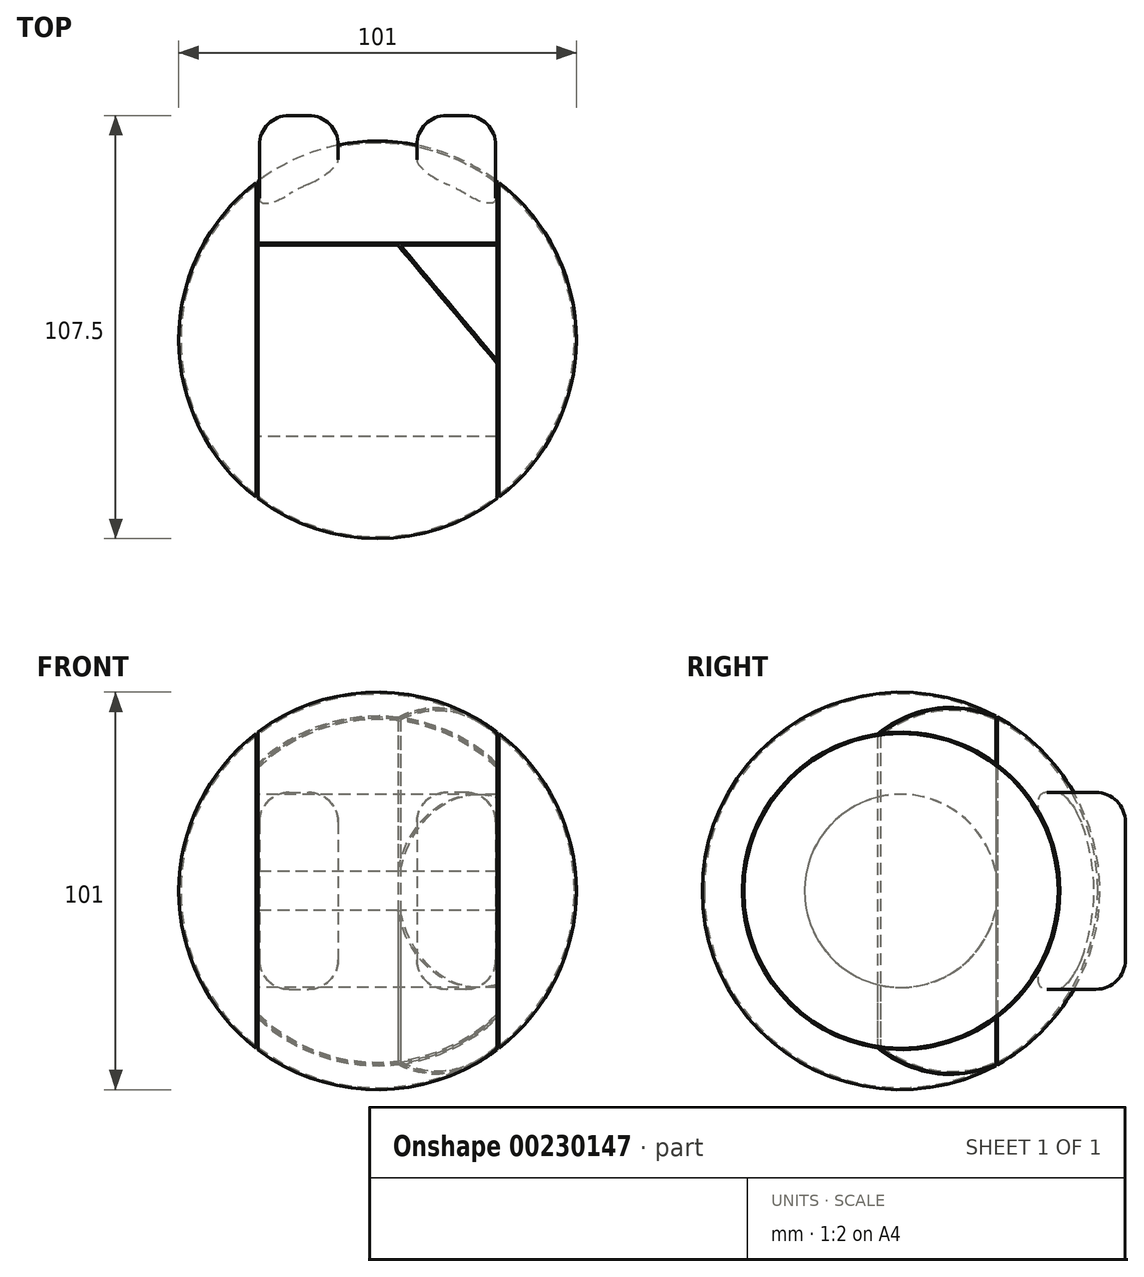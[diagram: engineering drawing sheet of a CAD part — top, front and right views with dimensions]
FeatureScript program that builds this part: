
annotation { "Feature Type Name" : "Feature", "Feature Type Description" : "" }
export const myFeature = defineFeature(function(context is Context, id is Id, definition is map)
    precondition{}
    {
        {
            var Q0;
            Q0=qCreatedBy(makeId("Top.planeOp"),FACE);
            var sketch = newSketch(context, id + "F0", { "sketchPlane" : qUnion([Q0])});
            skCircle(sketch, "E0", {"center": v(0, 0) * mm, "radius": 50 * mm});
            skLineSegment(sketch, "E1", {"start": v(0, 50) * mm, "end": v(0, -50) * mm});
            skSolve(sketch);
        }
        {
            var Q0;
            {var subQ0=sQuery(id+"F0.wireOp",EDGE,"E1");Q0=makeQuery(id+"F0.imprint","IMPRINT",FACE,{"disambiguationData":[TD([[makeQuery(id+"F0.imprint","IMPRINT",EDGE,{"derivedFrom":subQ0}),-1.0]])]});}
            var Q1;
            Q1=sQuery(id+"F0.wireOp",EDGE,"E1");
            revolve(context, id + "F1", {"entities" : qUnion([Q0]), "axis" : qUnion([Q1]), "revolveType" : RevolveType.FULL});
        }
        {
            var Q0;
            Q0=qCreatedBy(makeId("Front.planeOp"),FACE);
            var sketch = newSketch(context, id + "F2", { "sketchPlane" : qUnion([Q0])});
            skCircle(sketch, "E2", {"center": v(0, 0) * mm, "radius": 50 * mm});
            skLineSegment(sketch, "E3", {"start": v(22.5, 25) * mm, "end": v(-43.3, 25) * mm, "construction": true});
            skLineSegment(sketch, "E4", {"start": v(0, 50) * mm, "end": v(0, -50) * mm, "construction": true});
            skLineSegment(sketch, "E5", {"start": v(50, 0) * mm, "end": v(-50, 0) * mm, "construction": true});
            skLineSegment(sketch, "E6.bottom", {"start": v(30, 25) * mm, "end": v(17.5, 25) * mm});
            skLineSegment(sketch, "E6.top", {"start": v(22.5, -25) * mm, "end": v(17.5, -25) * mm});
            skLineSegment(sketch, "E6.left", {"start": v(30, 17.5) * mm, "end": v(30, -17.5) * mm});
            skLineSegment(sketch, "E6.right", {"start": v(10, 17.5) * mm, "end": v(10, -17.5) * mm});
            skPoint(sketch, "E7.newPointA", {"position": v(30, 25) * mm});
            skArc(sketch, "E7.filletArc", {"start": v(30, 17.5) * mm, "mid": v(27.8, 22.8) * mm, "end": v(22.5, 25) * mm});
            skPoint(sketch, "E8.visualSharp", {"position": v(10, 25) * mm});
            skArc(sketch, "E8.filletArc", {"start": v(17.5, 25) * mm, "mid": v(12.2, 22.8) * mm, "end": v(10, 17.5) * mm});
            skPoint(sketch, "E9.visualSharp", {"position": v(30, -25) * mm});
            skArc(sketch, "E9.filletArc", {"start": v(22.5, -25) * mm, "mid": v(27.8, -22.8) * mm, "end": v(30, -17.5) * mm});
            skPoint(sketch, "E10.visualSharp", {"position": v(10, -25) * mm});
            skArc(sketch, "E10.filletArc", {"start": v(10, -17.5) * mm, "mid": v(12.2, -22.8) * mm, "end": v(17.5, -25) * mm});
            skLineSegment(sketch, "E11.MirrorCS", {"start": v(-10, 17.5) * mm, "end": v(-10, -17.5) * mm});
            skLineSegment(sketch, "E12.MirrorCS", {"start": v(-30, 17.5) * mm, "end": v(-30, -17.5) * mm});
            skArc(sketch, "E13.MirrorCS", {"start": v(-30, 17.5) * mm, "mid": v(-27.8, 22.8) * mm, "end": v(-22.5, 25) * mm});
            skArc(sketch, "E14.MirrorCS", {"start": v(-17.5, 25) * mm, "mid": v(-12.2, 22.8) * mm, "end": v(-10, 17.5) * mm});
            skArc(sketch, "E15.MirrorCS", {"start": v(-22.5, -25) * mm, "mid": v(-27.8, -22.8) * mm, "end": v(-30, -17.5) * mm});
            skArc(sketch, "E16.MirrorCS", {"start": v(-10, -17.5) * mm, "mid": v(-12.2, -22.8) * mm, "end": v(-17.5, -25) * mm});
            skLineSegment(sketch, "E17.MirrorCS", {"start": v(-22.5, -25) * mm, "end": v(-17.5, -25) * mm});
            skLineSegment(sketch, "E18.MirrorCS", {"start": v(-30, 25) * mm, "end": v(-17.5, 25) * mm});
            skSolve(sketch);
        }
        {
            var Q0;
            Q0=makeQuery(id+"F2.imprint","IMPRINT",FACE,{"disambiguationData":[TD([[makeQuery(id+"F2.imprint","IMPRINT",EDGE,{"derivedFrom":sQuery(id+"F2.wireOp",EDGE,"E6.left")}),-1.0]])]});
            var Q1;
            Q1=makeQuery(id+"F2.imprint","IMPRINT",FACE,{"disambiguationData":[TD([[makeQuery(id+"F2.imprint","IMPRINT",EDGE,{"derivedFrom":sQuery(id+"F2.wireOp",EDGE,"E11.MirrorCS")}),-1.0]])]});
            extrude(context, id + "F3", {"entities" : qUnion([Q0, Q1]), "operationType" : NewBodyOperationType.ADD, "oppositeDirection" : true, "depth" : 57 * mm});
        }
        {
            var Q0;
            Q0=makeQuery(id+"F3.opExtrude","CAP_EDGE",EDGE,{"disambiguationData":[OSD([sQuery(id+"F2.wireOp",EDGE,"E6.right")])],"isStart":false});
            var Q1;
            Q1=makeQuery(id+"F3.opExtrude","CAP_EDGE",EDGE,{"disambiguationData":[OSD([sQuery(id+"F2.wireOp",EDGE,"E12.MirrorCS")])],"isStart":false});
            fillet(context, id + "F4", {"entities" : qUnion([Q0, Q1]), "radius" : 7.5 * mm, "tangentPropagation" : true, "allowEdgeOverflow" : false});
        }
        {
            var Q0;
            Q0=qCreatedBy(makeId("Top.planeOp"),FACE);
            var sketch = newSketch(context, id + "F5", { "sketchPlane" : qUnion([Q0])});
            skCircle(sketch, "E19", {"center": v(0, 0) * mm, "radius": 50.5 * mm});
            skLineSegment(sketch, "E20", {"start": v(0, 50.5) * mm, "end": v(0, -50.5) * mm, "construction": true});
            skLineSegment(sketch, "E21", {"start": v(-30.89, 39.95) * mm, "end": v(-30.89, -39.95) * mm});
            skLineSegment(sketch, "E22", {"start": v(-30.39, 40.33) * mm, "end": v(-30.39, -40.33) * mm});
            skLineSegment(sketch, "E23", {"start": v(-50.5, 0) * mm, "end": v(50.5, 0) * mm, "construction": true});
            skPoint(sketch, "E23.startSnap0", {"position": v(-30.39, 0) * mm});
            skLineSegment(sketch, "E24", {"start": v(-50.5, 0) * mm, "end": v(50.5, 0) * mm});
            skLineSegment(sketch, "E25.MirrorCS", {"start": v(30.39, 40.33) * mm, "end": v(30.39, -40.33) * mm});
            skLineSegment(sketch, "E26.MirrorCS", {"start": v(30.89, 39.95) * mm, "end": v(30.89, -39.95) * mm});
            skLineSegment(sketch, "E27", {"start": v(-30.39, 24.54) * mm, "end": v(30.39, 24.54) * mm});
            skLineSegment(sketch, "E28", {"start": v(-30.39, 24.04) * mm, "end": v(30.39, 24.04) * mm});
            skLineSegment(sketch, "E29", {"start": v(5.85, 24.04) * mm, "end": v(30.39, -5.24) * mm});
            skLineSegment(sketch, "E30", {"start": v(5.2, 24.04) * mm, "end": v(30.39, -6.02) * mm});
            skSolve(sketch);
        }
        {
            var Q0;
            {var subQ0=sQuery(id+"F5.wireOp",EDGE,"E21");var subQ1=sQuery(id+"F5.wireOp",EDGE,"E19");var subQ2=makeQuery(id+"F5.imprint","INTERSECT",VERTEX,{"disambiguationData":[OD(0.0)],"derivedFrom":[subQ1,subQ0]});Q0=makeQuery(id+"F5.imprint","IMPRINT",FACE,{"disambiguationData":[TD([[makeQuery(id+"F5.imprint","IMPRINT",EDGE,{"disambiguationData":[TD([[subQ2,-1.0]])],"derivedFrom":subQ1}),1.0]])]});}
            var Q1;
            {var subQ0=sQuery(id+"F5.wireOp",EDGE,"E24");var subQ1=sQuery(id+"F5.wireOp",EDGE,"E19");var subQ2=makeQuery(id+"F5.imprint","INTERSECT",VERTEX,{"disambiguationData":[OD(1.0)],"derivedFrom":[subQ1,subQ0]});Q1=makeQuery(id+"F5.imprint","IMPRINT",FACE,{"disambiguationData":[TD([[makeQuery(id+"F5.imprint","IMPRINT",EDGE,{"disambiguationData":[TD([[subQ2,-1.0]])],"derivedFrom":subQ1}),1.0]])]});}
            var Q2;
            {var subQ5=sQuery(id+"F5.wireOp",EDGE,"E27");Q2=makeQuery(id+"F5.imprint","IMPRINT",FACE,{"disambiguationData":[TD([[makeQuery(id+"F5.imprint","IMPRINT",EDGE,{"derivedFrom":subQ5}),1.0]])]});}
            var Q3;
            Q3=sQuery(id+"F5.wireOp",EDGE,"E24");
            revolve(context, id + "F6", {"entities" : qUnion([Q0, Q1, Q2]), "axis" : qUnion([Q3]), "revolveType" : RevolveType.FULL});
        }
        {
            var Q0;
            {var subQ0=sQuery(id+"F5.wireOp",EDGE,"E27");Q0=makeQuery(id+"F5.imprint","IMPRINT",FACE,{"disambiguationData":[TD([[makeQuery(id+"F5.imprint","IMPRINT",EDGE,{"derivedFrom":subQ0}),-1.0]])]});}
            var Q1;
            {var subQ0=sQuery(id+"F5.wireOp",EDGE,"E30");var subQ1=sQuery(id+"F5.wireOp",EDGE,"E24");var subQ2=makeQuery(id+"F5.imprint","INTERSECT",VERTEX,{"derivedFrom":[subQ1,subQ0]});Q1=makeQuery(id+"F5.imprint","IMPRINT",FACE,{"disambiguationData":[TD([[makeQuery(id+"F5.imprint","IMPRINT",EDGE,{"disambiguationData":[TD([[subQ2,-1.0]])],"derivedFrom":subQ1}),1.0]])]});}
            var Q2;
            {var subQ0=sQuery(id+"F5.wireOp",EDGE,"E30");var subQ1=sQuery(id+"F5.wireOp",EDGE,"E24");var subQ2=makeQuery(id+"F5.imprint","INTERSECT",VERTEX,{"derivedFrom":[subQ1,subQ0]});Q2=makeQuery(id+"F5.imprint","IMPRINT",FACE,{"disambiguationData":[TD([[makeQuery(id+"F5.imprint","IMPRINT",EDGE,{"disambiguationData":[TD([[subQ2,-1.0]])],"derivedFrom":subQ1}),-1.0]])]});}
            var Q3;
            {var subQ0=sQuery(id+"F5.wireOp",EDGE,"E19");Q3=makeQuery(id+"F6.opRevolve","SWEPT_FACE",FACE,{"disambiguationData":[OSD([subQ0]),TDD([makeQuery(id+"F5.imprint","IMPRINT",EDGE,{"disambiguationData":[TD([[makeQuery(id+"F5.imprint","INTERSECT",VERTEX,{"disambiguationData":[OD(0.0)],"derivedFrom":[subQ0,sQuery(id+"F5.wireOp",EDGE,"E22")]}),1.0]])],"derivedFrom":subQ0})])]});}
            var Q4;
            {var subQ0=sQuery(id+"F5.wireOp",EDGE,"E19");Q4=makeQuery(id+"F6.opRevolve","SWEPT_FACE",FACE,{"disambiguationData":[OSD([subQ0]),TDD([makeQuery(id+"F5.imprint","IMPRINT",EDGE,{"disambiguationData":[TD([[makeQuery(id+"F5.imprint","INTERSECT",VERTEX,{"disambiguationData":[OD(0.0)],"derivedFrom":[subQ0,sQuery(id+"F5.wireOp",EDGE,"E22")]}),1.0]])],"derivedFrom":subQ0})])]});}
            extrude(context, id + "F7", {"entities" : qUnion([Q0, Q1, Q2]), "operationType" : NewBodyOperationType.REMOVE, "endBound" : BoundingType.UP_TO_SURFACE, "endBoundEntityFace" : qUnion([Q3]), "depth" : 25 * mm, "hasSecondDirection" : true, "secondDirectionBound" : BoundingType.UP_TO_SURFACE, "secondDirectionOppositeDirection" : true, "secondDirectionBoundEntityFace" : qUnion([Q4]), "secondDirectionDepth" : 25 * mm});
        }
    });
